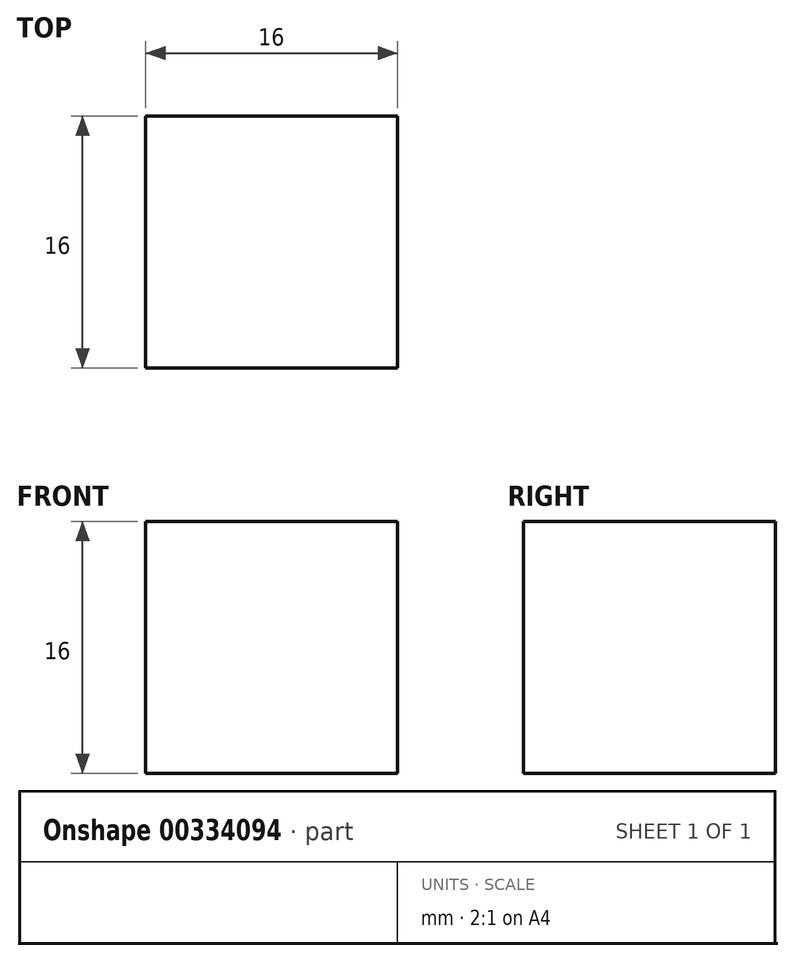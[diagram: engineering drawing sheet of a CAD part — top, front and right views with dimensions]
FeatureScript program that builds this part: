
annotation { "Feature Type Name" : "Feature", "Feature Type Description" : "" }
export const myFeature = defineFeature(function(context is Context, id is Id, definition is map)
    precondition{}
    {
        {
            var Q0;
            Q0=qCreatedBy(makeId("Top.planeOp"),FACE);
            var sketch = newSketch(context, id + "F0", { "sketchPlane" : qUnion([Q0])});
            skLineSegment(sketch, "E0.bottom", {"start": v(8, -8) * mm, "end": v(-8, -8) * mm});
            skLineSegment(sketch, "E0.top", {"start": v(8, 8) * mm, "end": v(-8, 8) * mm});
            skLineSegment(sketch, "E0.left", {"start": v(8, -8) * mm, "end": v(8, 8) * mm});
            skLineSegment(sketch, "E0.right", {"start": v(-8, -8) * mm, "end": v(-8, 8) * mm});
            skPoint(sketch, "E0.middle", {"position": v(0, 0) * mm});
            skSolve(sketch);
        }
        {
            var Q0;
            Q0=makeQuery(id+"F0.imprint","IMPRINT",FACE,{"disambiguationData":[TD([[makeQuery(id+"F0.imprint","IMPRINT",EDGE,{"derivedFrom":sQuery(id+"F0.wireOp",EDGE,"E0.bottom")}),-1.0]])]});
            extrude(context, id + "F1", {"entities" : qUnion([Q0]), "depth" : 16 * mm});
        }
    });
